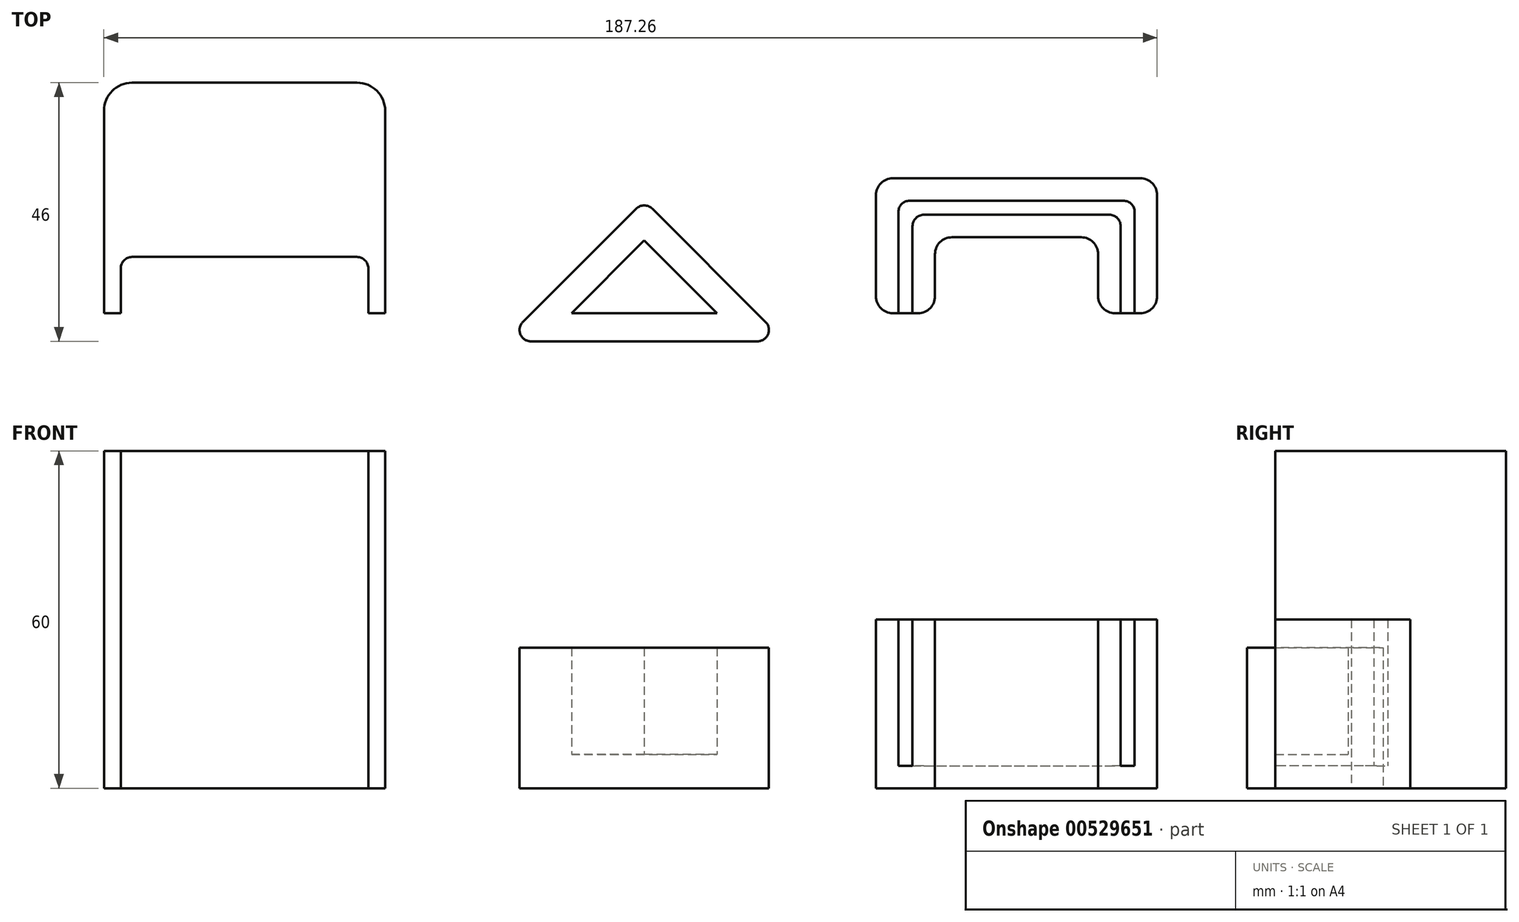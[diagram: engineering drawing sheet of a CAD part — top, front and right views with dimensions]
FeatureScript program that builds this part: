
annotation { "Feature Type Name" : "Feature", "Feature Type Description" : "" }
export const myFeature = defineFeature(function(context is Context, id is Id, definition is map)
    precondition{}
    {
        {
            var Q0;
            Q0=qCreatedBy(makeId("Top.planeOp"),FACE);
            var sketch = newSketch(context, id + "F0", { "sketchPlane" : qUnion([Q0])});
            skLineSegment(sketch, "E0", {"start": v(0, 20) * mm, "end": v(-25, -5) * mm});
            skLineSegment(sketch, "E1", {"start": v(-25, -5) * mm, "end": v(25, -5) * mm});
            skLineSegment(sketch, "E2", {"start": v(25, -5) * mm, "end": v(0, 20) * mm});
            skLineSegment(sketch, "E3.0", {"start": v(0, 12.93) * mm, "end": v(-12.93, 0) * mm});
            skLineSegment(sketch, "E3.1", {"start": v(12.93, 0) * mm, "end": v(0, 12.93) * mm});
            skLineSegment(sketch, "E3.2", {"start": v(-12.93, 0) * mm, "end": v(12.93, 0) * mm});
            skSolve(sketch);
        }
        {
            var Q0;
            Q0=makeQuery(id+"F0.imprint","IMPRINT",FACE,{"disambiguationData":[TD([[makeQuery(id+"F0.imprint","IMPRINT",EDGE,{"derivedFrom":sQuery(id+"F0.wireOp",EDGE,"E3.0")}),1.0]])]});
            extrude(context, id + "F1", {"entities" : qUnion([Q0]), "depth" : 6 * mm, "offsetDistance" : 25 * mm});
        }
        {
            var Q0;
            Q0=makeQuery(id+"F0.imprint","IMPRINT",FACE,{"disambiguationData":[TD([[makeQuery(id+"F0.imprint","IMPRINT",EDGE,{"derivedFrom":sQuery(id+"F0.wireOp",EDGE,"E0")}),1.0]])]});
            extrude(context, id + "F2", {"entities" : qUnion([Q0]), "operationType" : NewBodyOperationType.ADD, "depth" : 25 * mm, "offsetDistance" : 25 * mm});
        }
        {
            var Q0;
            Q0=makeQuery(id+"F2.opExtrude","SWEPT_EDGE",EDGE,{"disambiguationData":[OSD([sQuery(id+"F0.wireOp",EDGE,"E0"),sQuery(id+"F0.wireOp",EDGE,"E1")])]});
            var Q1;
            Q1=makeQuery(id+"F2.opExtrude","SWEPT_EDGE",EDGE,{"disambiguationData":[OSD([sQuery(id+"F0.wireOp",EDGE,"E1"),sQuery(id+"F0.wireOp",EDGE,"E2")])]});
            var Q2;
            Q2=makeQuery(id+"F2.opExtrude","SWEPT_EDGE",EDGE,{"disambiguationData":[OSD([sQuery(id+"F0.wireOp",EDGE,"E0"),sQuery(id+"F0.wireOp",EDGE,"E2")])]});
            fillet(context, id + "F3", {"entities" : qUnion([Q0, Q1, Q2]), "radius" : 2 * mm, "tangentPropagation" : true, "allowEdgeOverflow" : false});
        }
        {
            var Q0;
            Q0=qCreatedBy(makeId("Top.planeOp"),FACE);
            var sketch = newSketch(context, id + "F4", { "sketchPlane" : qUnion([Q0])});
            skLineSegment(sketch, "E4.bottom", {"start": v(-46.06, 0) * mm, "end": v(-49.06, 0) * mm});
            skLineSegment(sketch, "E4.top", {"start": v(-46.06, 41) * mm, "end": v(-96.06, 41) * mm});
            skLineSegment(sketch, "E4.left", {"start": v(-46.06, 0) * mm, "end": v(-46.06, 41) * mm});
            skLineSegment(sketch, "E4.right", {"start": v(-96.06, 0) * mm, "end": v(-96.06, 41) * mm});
            skLineSegment(sketch, "E5.top", {"start": v(-93.06, 10) * mm, "end": v(-49.06, 10) * mm});
            skLineSegment(sketch, "E5.left", {"start": v(-93.06, 0) * mm, "end": v(-93.06, 10) * mm});
            skLineSegment(sketch, "E5.right", {"start": v(-49.06, 0) * mm, "end": v(-49.06, 10) * mm});
            skLineSegment(sketch, "E6.trimOffspring", {"start": v(-93.06, 0) * mm, "end": v(-96.06, 0) * mm});
            skSolve(sketch);
        }
        {
            var Q0;
            Q0=makeQuery(id+"F4.imprint","IMPRINT",FACE,{"disambiguationData":[TD([[makeQuery(id+"F4.imprint","IMPRINT",EDGE,{"derivedFrom":sQuery(id+"F4.wireOp",EDGE,"E4.bottom")}),-1.0]])]});
            extrude(context, id + "F5", {"entities" : qUnion([Q0]), "depth" : 60 * mm, "offsetDistance" : 25 * mm});
        }
        {
            var Q0;
            Q0=makeQuery(id+"F5.opExtrude","SWEPT_EDGE",EDGE,{"disambiguationData":[OSD([sQuery(id+"F4.wireOp",EDGE,"E4.top"),sQuery(id+"F4.wireOp",EDGE,"E4.right")])]});
            var Q1;
            Q1=makeQuery(id+"F5.opExtrude","SWEPT_EDGE",EDGE,{"disambiguationData":[OSD([sQuery(id+"F4.wireOp",EDGE,"E4.top"),sQuery(id+"F4.wireOp",EDGE,"E4.left")])]});
            fillet(context, id + "F6", {"entities" : qUnion([Q0, Q1]), "radius" : 5 * mm, "tangentPropagation" : true, "allowEdgeOverflow" : false});
        }
        {
            var Q0;
            Q0=makeQuery(id+"F5.opExtrude","SWEPT_EDGE",EDGE,{"disambiguationData":[OSD([sQuery(id+"F4.wireOp",EDGE,"E5.top"),sQuery(id+"F4.wireOp",EDGE,"E5.left")])]});
            var Q1;
            Q1=makeQuery(id+"F5.opExtrude","SWEPT_EDGE",EDGE,{"disambiguationData":[OSD([sQuery(id+"F4.wireOp",EDGE,"E5.top"),sQuery(id+"F4.wireOp",EDGE,"E5.right")])]});
            fillet(context, id + "F7", {"entities" : qUnion([Q0, Q1]), "radius" : 2 * mm, "tangentPropagation" : true, "allowEdgeOverflow" : false});
        }
        {
            var Q0;
            Q0=qCreatedBy(makeId("Top.planeOp"),FACE);
            var sketch = newSketch(context, id + "F8", { "sketchPlane" : qUnion([Q0])});
            skLineSegment(sketch, "E7.bottom", {"start": v(45.2, 20) * mm, "end": v(87.2, 20) * mm});
            skLineSegment(sketch, "E7.top", {"start": v(45.2, 0) * mm, "end": v(87.2, 0) * mm});
            skLineSegment(sketch, "E7.left", {"start": v(45.2, 20) * mm, "end": v(45.2, 0) * mm});
            skLineSegment(sketch, "E7.right", {"start": v(87.2, 20) * mm, "end": v(87.2, 0) * mm});
            skLineSegment(sketch, "E8.0", {"start": v(47.7, 17.5) * mm, "end": v(47.7, 0) * mm});
            skLineSegment(sketch, "E8.1", {"start": v(47.7, 17.5) * mm, "end": v(84.7, 17.5) * mm});
            skLineSegment(sketch, "E8.2", {"start": v(84.7, 17.5) * mm, "end": v(84.7, 0) * mm});
            skLineSegment(sketch, "E9.bottom", {"start": v(41.2, 0) * mm, "end": v(91.2, 0) * mm});
            skLineSegment(sketch, "E9.top", {"start": v(41.2, 24) * mm, "end": v(91.2, 24) * mm});
            skLineSegment(sketch, "E9.left", {"start": v(41.2, 0) * mm, "end": v(41.2, 24) * mm});
            skLineSegment(sketch, "E9.right", {"start": v(91.2, 0) * mm, "end": v(91.2, 24) * mm});
            skLineSegment(sketch, "E10.bottom", {"start": v(51.7, 0) * mm, "end": v(80.7, 0) * mm});
            skLineSegment(sketch, "E10.top", {"start": v(51.7, 13.5) * mm, "end": v(80.7, 13.5) * mm});
            skLineSegment(sketch, "E10.left", {"start": v(51.7, 0) * mm, "end": v(51.7, 13.5) * mm});
            skLineSegment(sketch, "E10.right", {"start": v(80.7, 0) * mm, "end": v(80.7, 13.5) * mm});
            skSolve(sketch);
        }
        {
            var Q0;
            Q0=makeQuery(id+"F8.imprint","IMPRINT",FACE,{"disambiguationData":[TD([[makeQuery(id+"F8.imprint","IMPRINT",EDGE,{"derivedFrom":sQuery(id+"F8.wireOp",EDGE,"E7.bottom")}),-1.0]])]});
            extrude(context, id + "F9", {"entities" : qUnion([Q0]), "depth" : 4 * mm, "offsetDistance" : 25 * mm});
        }
        {
            var Q0;
            Q0=makeQuery(id+"F8.imprint","IMPRINT",FACE,{"disambiguationData":[TD([[makeQuery(id+"F8.imprint","IMPRINT",EDGE,{"derivedFrom":sQuery(id+"F8.wireOp",EDGE,"E7.bottom")}),1.0]])]});
            var Q1;
            {var subQ2=sQuery(id+"F8.wireOp",EDGE,"E8.0");Q1=makeQuery(id+"F8.imprint","IMPRINT",FACE,{"disambiguationData":[TD([[makeQuery(id+"F8.imprint","IMPRINT",EDGE,{"derivedFrom":subQ2}),1.0]])]});}
            extrude(context, id + "F10", {"entities" : qUnion([Q0, Q1]), "operationType" : NewBodyOperationType.ADD, "depth" : 30 * mm, "offsetDistance" : 25 * mm});
        }
        {
            var Q0;
            Q0=makeQuery(id+"F10.opExtrude","SWEPT_EDGE",EDGE,{"disambiguationData":[OSD([sQuery(id+"F8.wireOp",EDGE,"E9.top"),sQuery(id+"F8.wireOp",EDGE,"E9.right")])]});
            var Q1;
            Q1=makeQuery(id+"F10.opExtrude","SWEPT_EDGE",EDGE,{"disambiguationData":[OSD([sQuery(id+"F8.wireOp",EDGE,"E9.top"),sQuery(id+"F8.wireOp",EDGE,"E9.left")])]});
            var Q2;
            Q2=makeQuery(id+"F10.opExtrude","SWEPT_EDGE",EDGE,{"disambiguationData":[OSD([sQuery(id+"F8.wireOp",EDGE,"E10.top"),sQuery(id+"F8.wireOp",EDGE,"E10.left")])]});
            var Q3;
            Q3=makeQuery(id+"F10.opExtrude","SWEPT_EDGE",EDGE,{"disambiguationData":[OSD([sQuery(id+"F8.wireOp",EDGE,"E10.top"),sQuery(id+"F8.wireOp",EDGE,"E10.right")])]});
            var Q4;
            Q4=makeQuery(id+"F10.opExtrude","SWEPT_EDGE",EDGE,{"disambiguationData":[OSD([sQuery(id+"F8.wireOp",EDGE,"E9.bottom"),sQuery(id+"F8.wireOp",EDGE,"E9.left")])]});
            var Q5;
            Q5=makeQuery(id+"F10.opExtrude","SWEPT_EDGE",EDGE,{"disambiguationData":[OSD([sQuery(id+"F8.wireOp",EDGE,"E9.bottom"),sQuery(id+"F8.wireOp",EDGE,"E10.bottom"),sQuery(id+"F8.wireOp",EDGE,"E10.left")])]});
            var Q6;
            Q6=makeQuery(id+"F10.opExtrude","SWEPT_EDGE",EDGE,{"disambiguationData":[OSD([sQuery(id+"F8.wireOp",EDGE,"E9.bottom"),sQuery(id+"F8.wireOp",EDGE,"E10.bottom"),sQuery(id+"F8.wireOp",EDGE,"E10.right")])]});
            var Q7;
            Q7=makeQuery(id+"F10.opExtrude","SWEPT_EDGE",EDGE,{"disambiguationData":[OSD([sQuery(id+"F8.wireOp",EDGE,"E9.bottom"),sQuery(id+"F8.wireOp",EDGE,"E9.right")])]});
            fillet(context, id + "F11", {"entities" : qUnion([Q0, Q1, Q2, Q3, Q4, Q5, Q6, Q7]), "radius" : 3 * mm, "tangentPropagation" : true, "allowEdgeOverflow" : false});
        }
        {
            var Q0;
            Q0=makeQuery(id+"F10.opExtrude","SWEPT_EDGE",EDGE,{"disambiguationData":[OSD([sQuery(id+"F8.wireOp",EDGE,"E7.bottom"),sQuery(id+"F8.wireOp",EDGE,"E7.left")])]});
            var Q1;
            Q1=makeQuery(id+"F10.opExtrude","SWEPT_EDGE",EDGE,{"disambiguationData":[OSD([sQuery(id+"F8.wireOp",EDGE,"E8.0"),sQuery(id+"F8.wireOp",EDGE,"E8.1")])]});
            var Q2;
            Q2=makeQuery(id+"F10.opExtrude","SWEPT_EDGE",EDGE,{"disambiguationData":[OSD([sQuery(id+"F8.wireOp",EDGE,"E7.bottom"),sQuery(id+"F8.wireOp",EDGE,"E7.right")])]});
            var Q3;
            Q3=makeQuery(id+"F10.opExtrude","SWEPT_EDGE",EDGE,{"disambiguationData":[OSD([sQuery(id+"F8.wireOp",EDGE,"E8.1"),sQuery(id+"F8.wireOp",EDGE,"E8.2")])]});
            fillet(context, id + "F12", {"entities" : qUnion([Q0, Q1, Q2, Q3]), "radius" : 2 * mm, "tangentPropagation" : true, "allowEdgeOverflow" : false});
        }
    });
